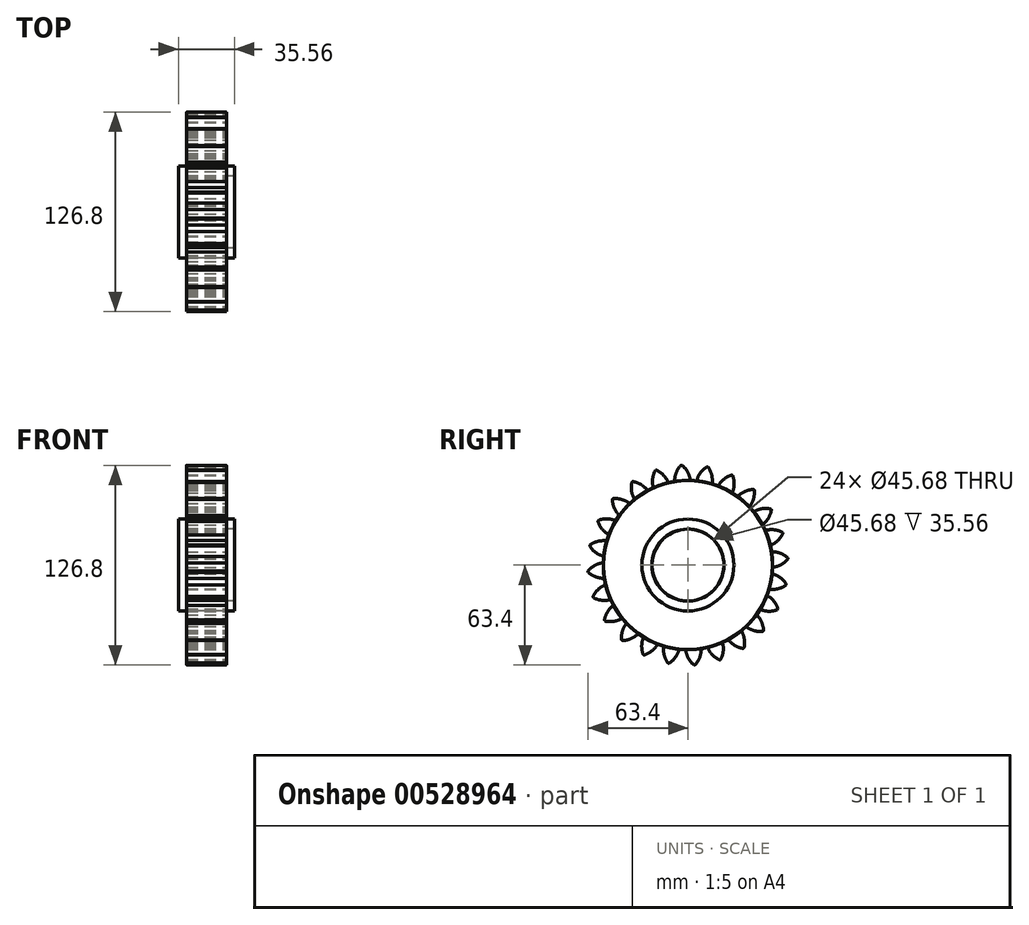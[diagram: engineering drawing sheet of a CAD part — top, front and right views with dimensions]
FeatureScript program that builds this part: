
annotation { "Feature Type Name" : "Feature", "Feature Type Description" : "" }
export const myFeature = defineFeature(function(context is Context, id is Id, definition is map)
    precondition{}
    {
        {
            var Q0;
            Q0=qCreatedBy(makeId("Right.planeOp"),FACE);
            var sketch = newSketch(context, id + "F0", { "sketchPlane" : qUnion([Q0])});
            skCircle(sketch, "E0", {"center": v(0, 0) * mm, "radius": 22.84 * mm});
            skCircle(sketch, "E1", {"center": v(0, 0) * mm, "radius": 53.72 * mm});
            skCircle(sketch, "E2", {"center": v(0, 0) * mm, "radius": 53.72 * mm, "construction": true});
            skCircle(sketch, "E3", {"center": v(0, 0) * mm, "radius": 58.67 * mm, "construction": true});
            skCircle(sketch, "E4", {"center": v(0, 0) * mm, "radius": 63.5 * mm, "construction": true});
            skLineSegment(sketch, "E5", {"start": v(0, 0) * mm, "end": v(0, 95.03) * mm, "construction": true});
            skLineSegment(sketch, "E6", {"start": v(0, 0) * mm, "end": v(-6.2, 94.63) * mm, "construction": true});
            skLineSegment(sketch, "E7", {"start": v(0, 58.67) * mm, "end": v(-92.9, 58.67) * mm, "construction": true});
            skLineSegment(sketch, "E8", {"start": v(0, 58.67) * mm, "end": v(-91.75, 25.28) * mm, "construction": true});
            skCircle(sketch, "E9", {"center": v(0, 58.67) * mm, "radius": 14.6 * mm, "construction": true});
            skCircle(sketch, "E10", {"center": v(-13.05, 52.11) * mm, "radius": 14.6 * mm, "construction": true});
            skArc(sketch, "E11", {"start": v(0, 58.67) * mm, "mid": v(-1.64, 61.23) * mm, "end": v(-3.77, 63.39) * mm});
            skArc(sketch, "E12", {"start": v(1.47, 53.7) * mm, "mid": v(0.96, 56.25) * mm, "end": v(0, 58.67) * mm});
            skArc(sketch, "E13.MirrorCS", {"start": v(-7.66, 58.17) * mm, "mid": v(-6.37, 60.92) * mm, "end": v(-4.54, 63.34) * mm});
            skArc(sketch, "E14.MirrorCS", {"start": v(-8.47, 53.05) * mm, "mid": v(-8.3, 55.65) * mm, "end": v(-7.66, 58.17) * mm});
            skArc(sketch, "E15", {"start": v(-3.77, 63.39) * mm, "mid": v(-4.16, 63.4) * mm, "end": v(-4.54, 63.34) * mm});
            skSolve(sketch);
        }
        {
            var Q0;
            Q0=makeQuery(id+"F0.imprint","IMPRINT",FACE,{"disambiguationData":[TD([[makeQuery(id+"F0.imprint","IMPRINT",EDGE,{"derivedFrom":sQuery(id+"F0.wireOp",EDGE,"E11")}),1.0]])]});
            var Q1;
            {var subQ0=sQuery(id+"F0.wireOp",EDGE,"E1");var subQ1=makeQuery(id+"F0.imprint","INTERSECT",VERTEX,{"derivedFrom":[subQ0,sQuery(id+"F0.wireOp",EDGE,"E12")]});Q1=makeQuery(id+"F0.imprint","IMPRINT",FACE,{"disambiguationData":[TD([[makeQuery(id+"F0.imprint","IMPRINT",EDGE,{"disambiguationData":[TD([[subQ1,1.0]])],"derivedFrom":subQ0}),1.0]])]});}
            var Q2;
            Q2=makeQuery(id+"F0.imprint","IMPRINT",FACE,{"disambiguationData":[TD([[makeQuery(id+"F0.imprint","IMPRINT",EDGE,{"derivedFrom":sQuery(id+"F0.wireOp",EDGE,"E0")}),-1.0]])]});
            extrude(context, id + "F1", {"entities" : qUnion([Q0, Q1, Q2]), "oppositeDirection" : true, "depth" : 25.4 * mm, "offsetDistance" : 25.4 * mm});
        }
        {
            var Q0;
            Q0=makeQuery(id+"F1.opExtrude","SWEPT_BODY",BODY,{"disambiguationData":[OSD([sQuery(id+"F0.wireOp",EDGE,"E0"),sQuery(id+"F0.wireOp",EDGE,"E1"),sQuery(id+"F0.wireOp",EDGE,"E11"),sQuery(id+"F0.wireOp",EDGE,"E12"),sQuery(id+"F0.wireOp",EDGE,"E13.MirrorCS"),sQuery(id+"F0.wireOp",EDGE,"E14.MirrorCS"),sQuery(id+"F0.wireOp",EDGE,"E15")])]});
            var Q1;
            Q1=makeQuery(id+"F1.opExtrude","SWEPT_FACE",FACE,{"disambiguationData":[OSD([sQuery(id+"F0.wireOp",EDGE,"E1")])]});
            circularPattern(context, id + "F2", {"entities" : qUnion([Q0]), "axis" : qUnion([Q1]), "angle" : 360 * degree, "instanceCount" : 24, "oppositeDirection" : true, "equalSpace" : true});
        }
        {
            var Q0;
            Q0=makeQuery(id+"F2.opPattern","COPY",FACE,{"derivedFrom":makeQuery(id+"F1.opExtrude","CAP_FACE",FACE,{"disambiguationData":[OSD([sQuery(id+"F0.wireOp",EDGE,"E0"),sQuery(id+"F0.wireOp",EDGE,"E1"),sQuery(id+"F0.wireOp",EDGE,"E11"),sQuery(id+"F0.wireOp",EDGE,"E12"),sQuery(id+"F0.wireOp",EDGE,"E13.MirrorCS"),sQuery(id+"F0.wireOp",EDGE,"E14.MirrorCS"),sQuery(id+"F0.wireOp",EDGE,"E15")])],"isStart":true}),"instanceName":"2"});
            var sketch = newSketch(context, id + "F3", { "sketchPlane" : qUnion([Q0])});
            skCircle(sketch, "E16", {"center": v(0, 0) * mm, "radius": 29.19 * mm});
            skCircle(sketch, "E17", {"center": v(0, 0) * mm, "radius": 45.99 * mm});
            skSolve(sketch);
        }
        {
            var Q0;
            Q0=makeQuery(id+"F3.imprint","IMPRINT",FACE,{"disambiguationData":[TD([[makeQuery(id+"F3.imprint","IMPRINT",EDGE,{"derivedFrom":sQuery(id+"F3.wireOp",EDGE,"E16")}),1.0]])]});
            extrude(context, id + "F4", {"entities" : qUnion([Q0]), "depth" : 5.08 * mm, "offsetDistance" : 25.4 * mm, "hasSecondDirection" : true, "secondDirectionOppositeDirection" : true, "secondDirectionDepth" : 30.48 * mm});
        }
    });
